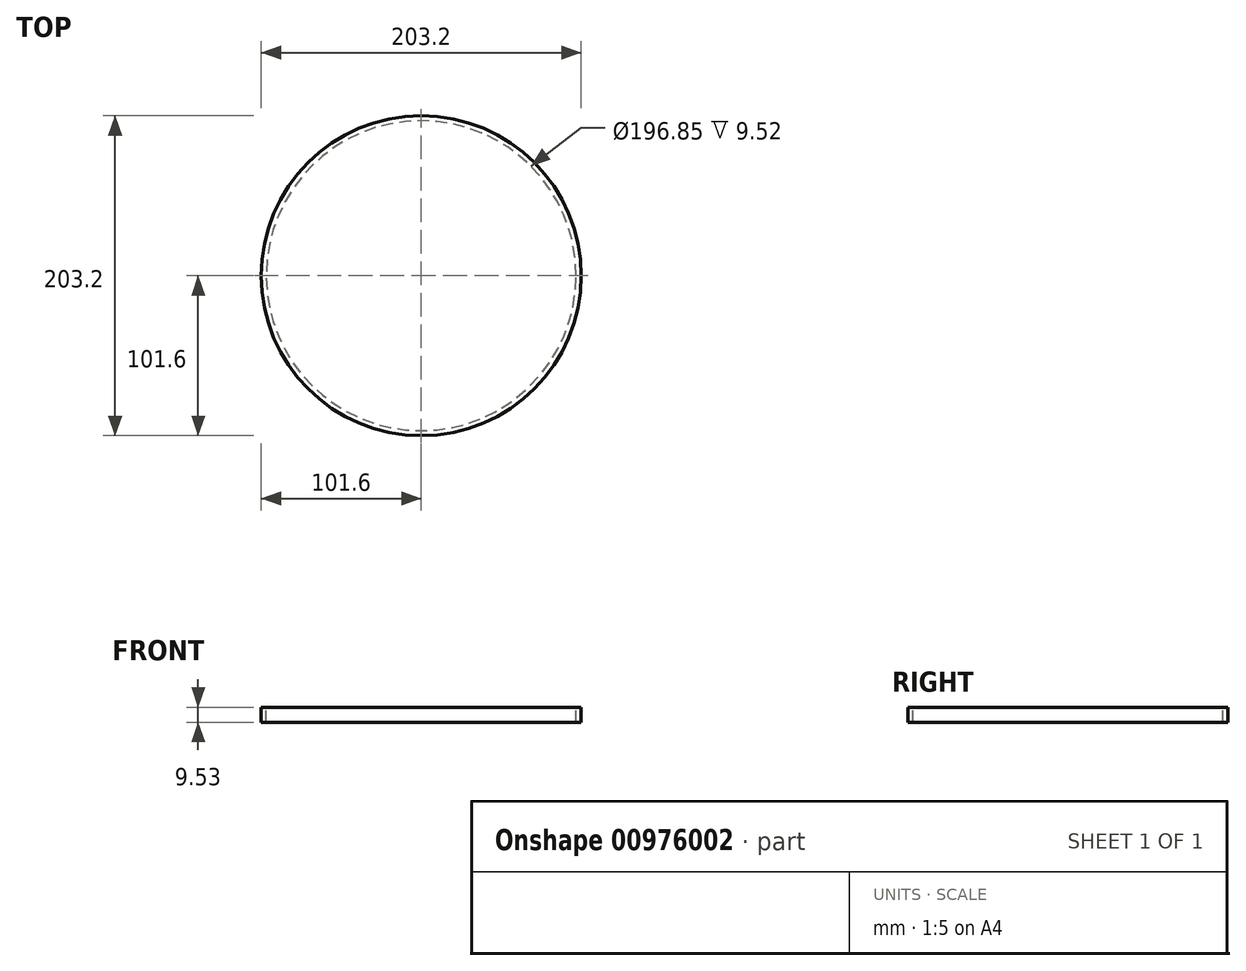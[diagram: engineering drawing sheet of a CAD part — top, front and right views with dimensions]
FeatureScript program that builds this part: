
annotation { "Feature Type Name" : "Feature", "Feature Type Description" : "" }
export const myFeature = defineFeature(function(context is Context, id is Id, definition is map)
    precondition{}
    {
        {
            var Q0;
            Q0=qCreatedBy(makeId("Top.planeOp"),FACE);
            var sketch = newSketch(context, id + "F0", { "sketchPlane" : qUnion([Q0])});
            skCircle(sketch, "E0", {"center": v(0, 0) * mm, "radius": 101.6 * mm});
            skCircle(sketch, "E1", {"center": v(0, 0) * mm, "radius": 98.43 * mm});
            skSolve(sketch);
        }
        {
            var Q0;
            Q0=makeQuery(id+"F0.imprint","IMPRINT",FACE,{"disambiguationData":[TD([[makeQuery(id+"F0.imprint","IMPRINT",EDGE,{"derivedFrom":sQuery(id+"F0.wireOp",EDGE,"E0")}),1.0]])]});
            extrude(context, id + "F1", {"entities" : qUnion([Q0]), "oppositeDirection" : true, "depth" : 9.52 * mm, "offsetDistance" : 25.4 * mm});
        }
        {
            var Q0;
            Q0=qCreatedBy(makeId("Top.planeOp"),FACE);
            var sketch = newSketch(context, id + "F2", { "sketchPlane" : qUnion([Q0])});
            skCircle(sketch, "E2", {"center": v(0, 0) * mm, "radius": 98.43 * mm});
            skSolve(sketch);
        }
        {
            var Q0;
            Q0=qSketchRegion(id+"F2",true);
            var Q1;
            Q1=makeQuery(id+"F2.imprint","IMPRINT",FACE,{"disambiguationData":[TD([[makeQuery(id+"F2.imprint","IMPRINT",EDGE,{"derivedFrom":sQuery(id+"F2.wireOp",EDGE,"E2")}),1.0]])]});
            extrude(context, id + "F3", {"entities" : qUnion([Q0, Q1]), "operationType" : NewBodyOperationType.ADD, "oppositeDirection" : true, "depth" : 1 / 203.2 * mm, "offsetDistance" : 25.4 * mm});
        }
    });
